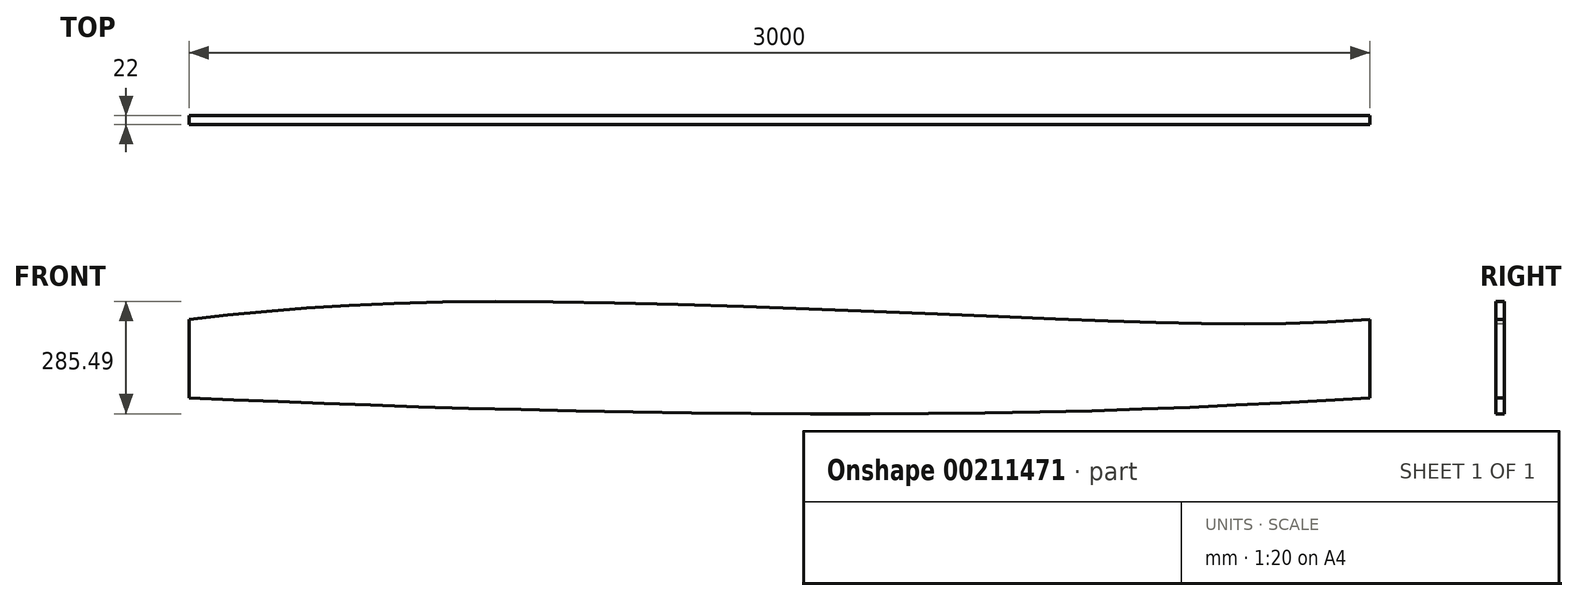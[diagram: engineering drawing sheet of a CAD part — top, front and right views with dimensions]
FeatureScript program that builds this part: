
annotation { "Feature Type Name" : "Feature", "Feature Type Description" : "" }
export const myFeature = defineFeature(function(context is Context, id is Id, definition is map)
    precondition{}
    {
        {
            var Q0;
            Q0=qCreatedBy(makeId("Front.planeOp"),FACE);
            var sketch = newSketch(context, id + "F0", { "sketchPlane" : qUnion([Q0])});
            skLineSegment(sketch, "E0.bottom", {"start": v(1528.02, 100) * mm, "end": v(-1471.98, 100) * mm, "construction": true});
            skLineSegment(sketch, "E0.top", {"start": v(1528.02, -100) * mm, "end": v(-1471.98, -100) * mm, "construction": true});
            skLineSegment(sketch, "E0.left", {"start": v(1528.02, 100) * mm, "end": v(1528.02, -100) * mm, "construction": true});
            skLineSegment(sketch, "E0.right", {"start": v(-1471.98, 100) * mm, "end": v(-1471.98, -100) * mm, "construction": true});
            skPoint(sketch, "E0.middle", {"position": v(28.02, 0) * mm});
            skLineSegment(sketch, "E1", {"start": v(-1471.98, 100) * mm, "end": v(-1471.98, -100) * mm});
            skLineSegment(sketch, "E2", {"start": v(1528.02, 100) * mm, "end": v(1528.02, -100) * mm});
            skFitSpline(sketch, "E3", {"points": [v(-1471.98, 100) * mm, v(-742.23, 145) * mm, v(747.3, 100) * mm, v(1528.02, 100) * mm], "startDerivative": vector(2262.87, 251.46) * mm, "endDerivative": vector(2511.41, 179.87) * mm});
            skFitSpline(sketch, "E4", {"points": [v(-1471.98, -100) * mm, v(-604.67, -130.1) * mm, v(673.05, -136.22) * mm, v(1528.02, -100) * mm], "startDerivative": vector(2594.1, -107.22) * mm, "endDerivative": vector(2571.13, 143.98) * mm});
            skSolve(sketch);
        }
        {
            var Q0;
            Q0 = qSketchRegion(id + "F0", true);
            extrude(context, id + "F1", {"entities" : qUnion([Q0]), "depth" : 22 * mm});
        }
    });
